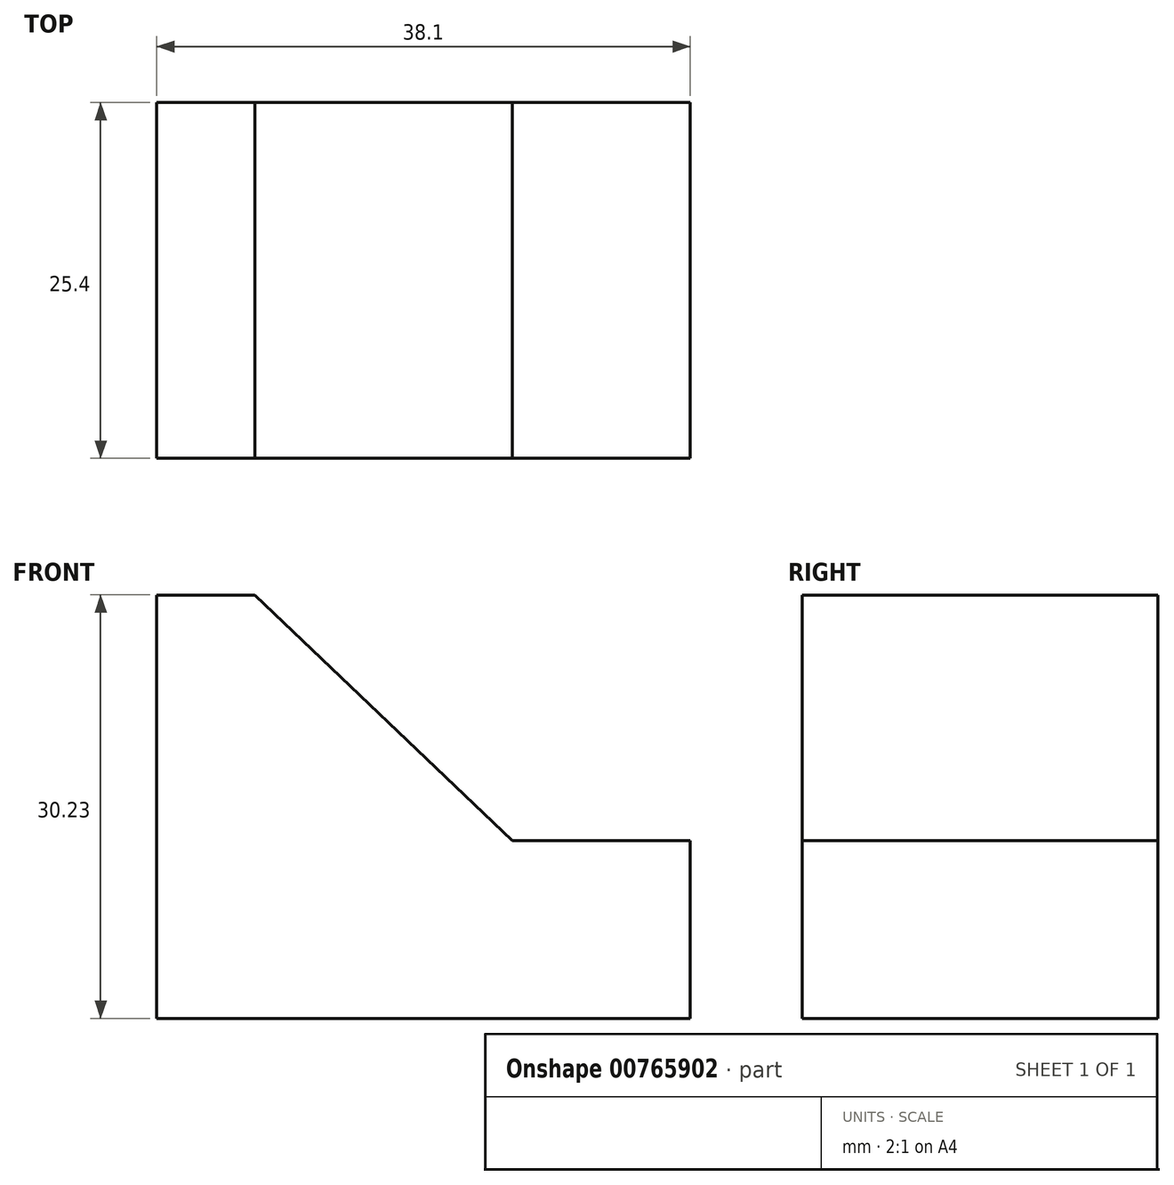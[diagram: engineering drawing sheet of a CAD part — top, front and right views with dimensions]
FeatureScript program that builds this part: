
annotation { "Feature Type Name" : "Feature", "Feature Type Description" : "" }
export const myFeature = defineFeature(function(context is Context, id is Id, definition is map)
    precondition{}
    {
        {
            var Q0;
            Q0=qCreatedBy(makeId("Front.planeOp"),FACE);
            var sketch = newSketch(context, id + "F0", { "sketchPlane" : qUnion([Q0])});
            skLineSegment(sketch, "E0", {"start": v(0, 0) * mm, "end": v(38.1, 0) * mm});
            skLineSegment(sketch, "E1", {"start": v(38.1, 0) * mm, "end": v(38.1, 12.7) * mm});
            skLineSegment(sketch, "E2", {"start": v(38.1, 12.7) * mm, "end": v(25.4, 12.7) * mm});
            skLineSegment(sketch, "E3", {"start": v(25.4, 12.7) * mm, "end": v(7.02, 30.23) * mm});
            skLineSegment(sketch, "E4", {"start": v(7.02, 30.23) * mm, "end": v(0, 30.23) * mm});
            skLineSegment(sketch, "E5", {"start": v(0, 30.23) * mm, "end": v(0, 0) * mm});
            skSolve(sketch);
        }
        {
            var Q0;
            Q0 = qSketchRegion(id + "F0", true);
            extrude(context, id + "F1", {"entities" : qUnion([Q0]), "depth" : 25.4 * mm, "offsetDistance" : 25.4 * mm});
        }
    });
